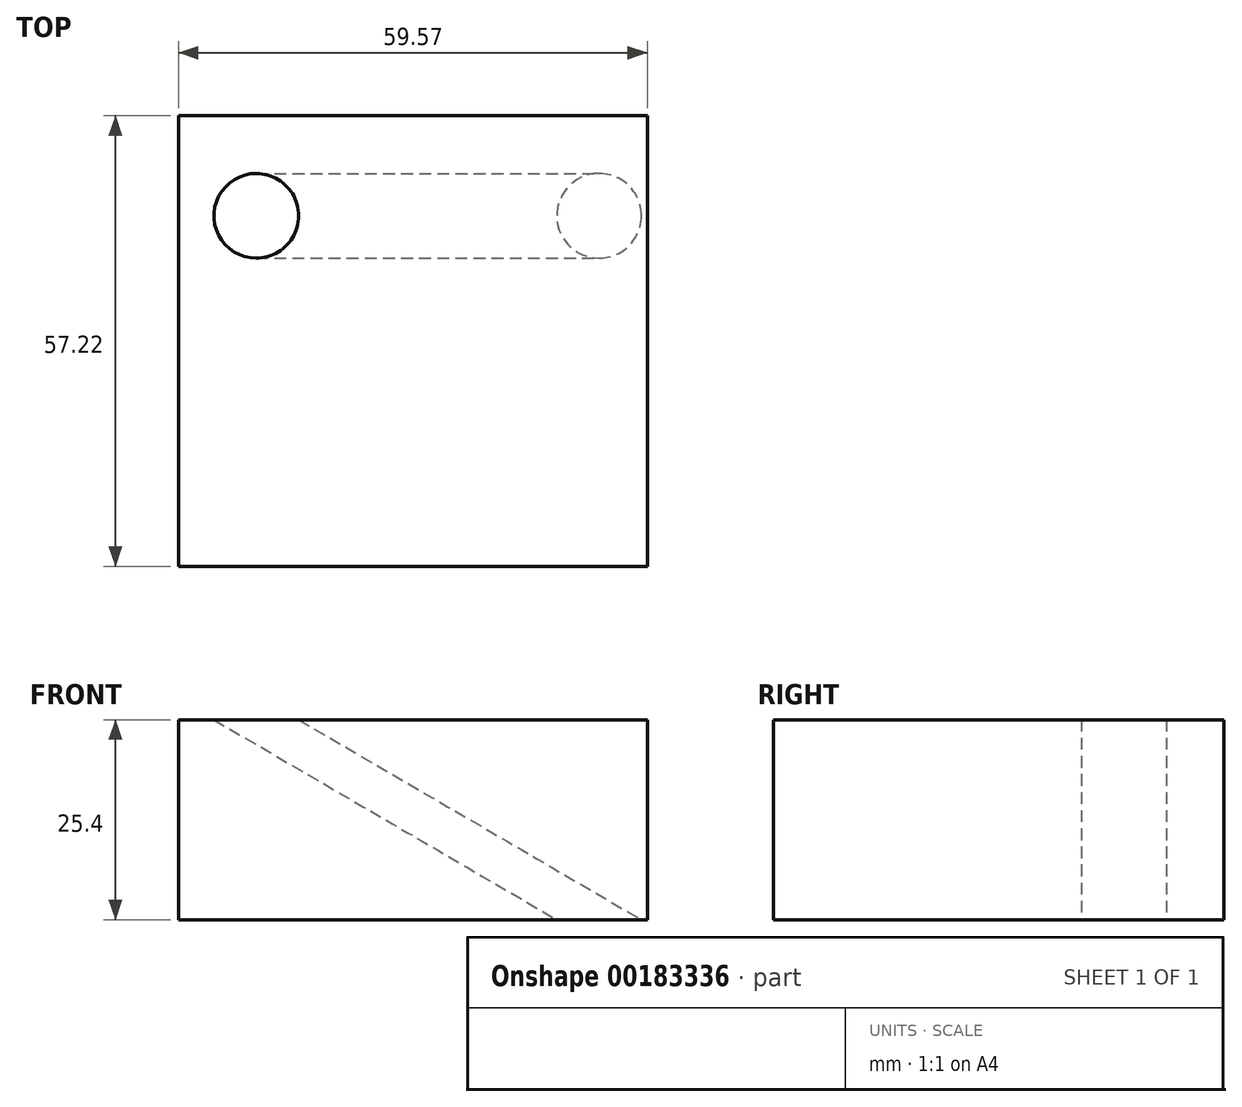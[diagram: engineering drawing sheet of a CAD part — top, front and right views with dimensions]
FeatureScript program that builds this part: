
annotation { "Feature Type Name" : "Feature", "Feature Type Description" : "" }
export const myFeature = defineFeature(function(context is Context, id is Id, definition is map)
    precondition{}
    {
        {
            var Q0;
            Q0=qCreatedBy(makeId("Top.planeOp"),FACE);
            var sketch = newSketch(context, id + "F0", { "sketchPlane" : qUnion([Q0])});
            skLineSegment(sketch, "E0.bottom", {"start": v(0, 0) * mm, "end": v(59.57, 0) * mm});
            skLineSegment(sketch, "E0.top", {"start": v(0, -57.22) * mm, "end": v(59.57, -57.22) * mm});
            skLineSegment(sketch, "E0.left", {"start": v(0, 0) * mm, "end": v(0, -57.22) * mm});
            skLineSegment(sketch, "E0.right", {"start": v(59.57, 0) * mm, "end": v(59.57, -57.22) * mm});
            skSolve(sketch);
        }
        {
            var Q0;
            Q0=makeQuery(id+"F0.imprint","IMPRINT",FACE,{"disambiguationData":[TD([[makeQuery(id+"F0.imprint","IMPRINT",EDGE,{"derivedFrom":sQuery(id+"F0.wireOp",EDGE,"E0.bottom")}),-1.0]])]});
            extrude(context, id + "F1", {"entities" : qUnion([Q0]), "depth" : 25.4 * mm});
        }
        {
            var Q0;
            Q0=makeQuery(id+"F1.opExtrude","CAP_FACE",FACE,{"disambiguationData":[OSD([sQuery(id+"F0.wireOp",EDGE,"E0.bottom"),sQuery(id+"F0.wireOp",EDGE,"E0.top"),sQuery(id+"F0.wireOp",EDGE,"E0.left"),sQuery(id+"F0.wireOp",EDGE,"E0.right")])],"isStart":false});
            var sketch = newSketch(context, id + "F2", { "sketchPlane" : qUnion([Q0])});
            skCircle(sketch, "E1", {"center": v(9.9, -12.7) * mm, "radius": 5.38 * mm});
            skLineSegment(sketch, "E2", {"start": v(9.9, -12.7) * mm, "end": v(9.9, 0) * mm, "construction": true});
            skLineSegment(sketch, "E3", {"start": v(0, -12.7) * mm, "end": v(59.57, -12.7) * mm, "construction": true});
            skSolve(sketch);
        }
        {
            var Q0;
            Q0=makeQuery(id+"F1.opExtrude","SWEPT_FACE",FACE,{"disambiguationData":[OSD([sQuery(id+"F0.wireOp",EDGE,"E0.bottom")])]});
            cPlane(context, id + "F3", {"entities" : qUnion([Q0]), "cplaneType" : CPlaneType.OFFSET, "offset" : 12.7 * mm, "oppositeDirection" : true, "width" : 152.4 * mm, "height" : 152.4 * mm});
        }
        {
            var Q0;
            Q0=qCreatedBy(id+"F3.planeOp",FACE);
            var sketch = newSketch(context, id + "F4", { "sketchPlane" : qUnion([Q0])});
            skLineSegment(sketch, "E4", {"start": v(-9.9, 25.96) * mm, "end": v(-54.4, 0) * mm});
            skSolve(sketch);
        }
        {
            var Q0;
            Q0=makeQuery(id+"F2.imprint","IMPRINT",FACE,{"disambiguationData":[TD([[makeQuery(id+"F2.imprint","IMPRINT",EDGE,{"derivedFrom":sQuery(id+"F2.wireOp",EDGE,"E1")}),1.0]])]});
            var Q1;
            Q1=sQuery(id+"F4.wireOp",EDGE,"E4");
            var Q2;
            Q2=sQuery(id+"F2.wireOp",EDGE,"E1");
            var Q3;
            Q3 = qConstructionFilter(qBodyType(qCreatedBy(id + "F4" ,EDGE), BodyType.WIRE), ConstructionObject.NO);
            sweep(context, id + "F5", {"operationType" : NewBodyOperationType.REMOVE, "profiles" : qUnion([Q0]), "surfaceProfiles" : qUnion([Q1, Q2]), "path" : qUnion([Q3])});
        }
    });
